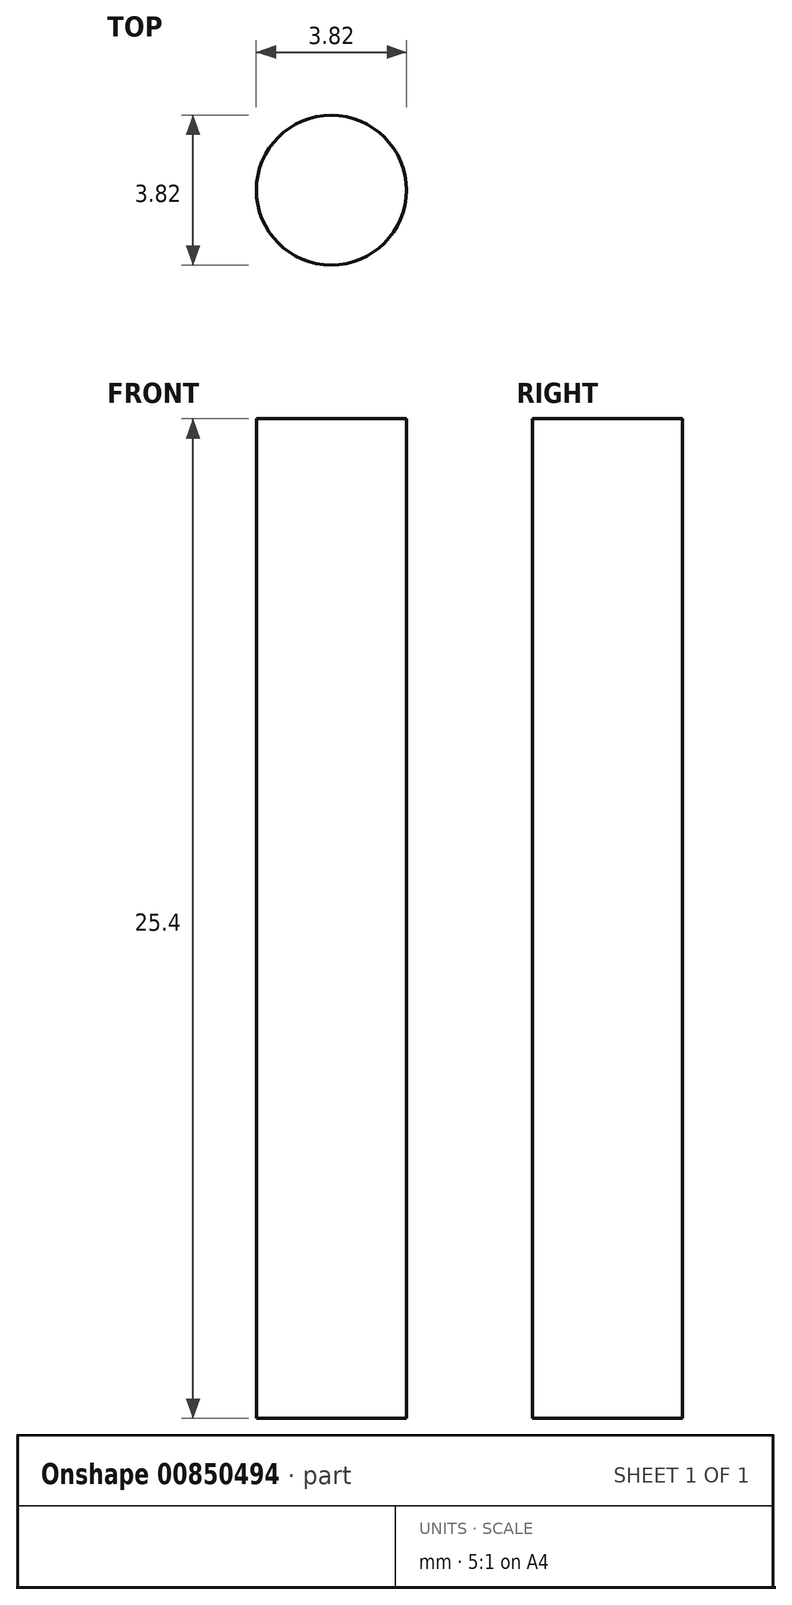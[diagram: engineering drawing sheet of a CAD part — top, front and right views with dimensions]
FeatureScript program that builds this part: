
annotation { "Feature Type Name" : "Feature", "Feature Type Description" : "" }
export const myFeature = defineFeature(function(context is Context, id is Id, definition is map)
    precondition{}
    {
        {
            var Q0;
            Q0=qCreatedBy(makeId("Top.planeOp"),FACE);
            var sketch = newSketch(context, id + "F0", { "sketchPlane" : qUnion([Q0])});
            skCircle(sketch, "E0", {"center": v(0, 0) * mm, "radius": 1.9 * mm});
            skSolve(sketch);
        }
        {
            var Q0;
            Q0 = qSketchRegion(id + "F0", true);
            extrude(context, id + "F1", {"entities" : qUnion([Q0]), "depth" : 25.4 * mm, "offsetDistance" : 25.4 * mm});
        }
    });
